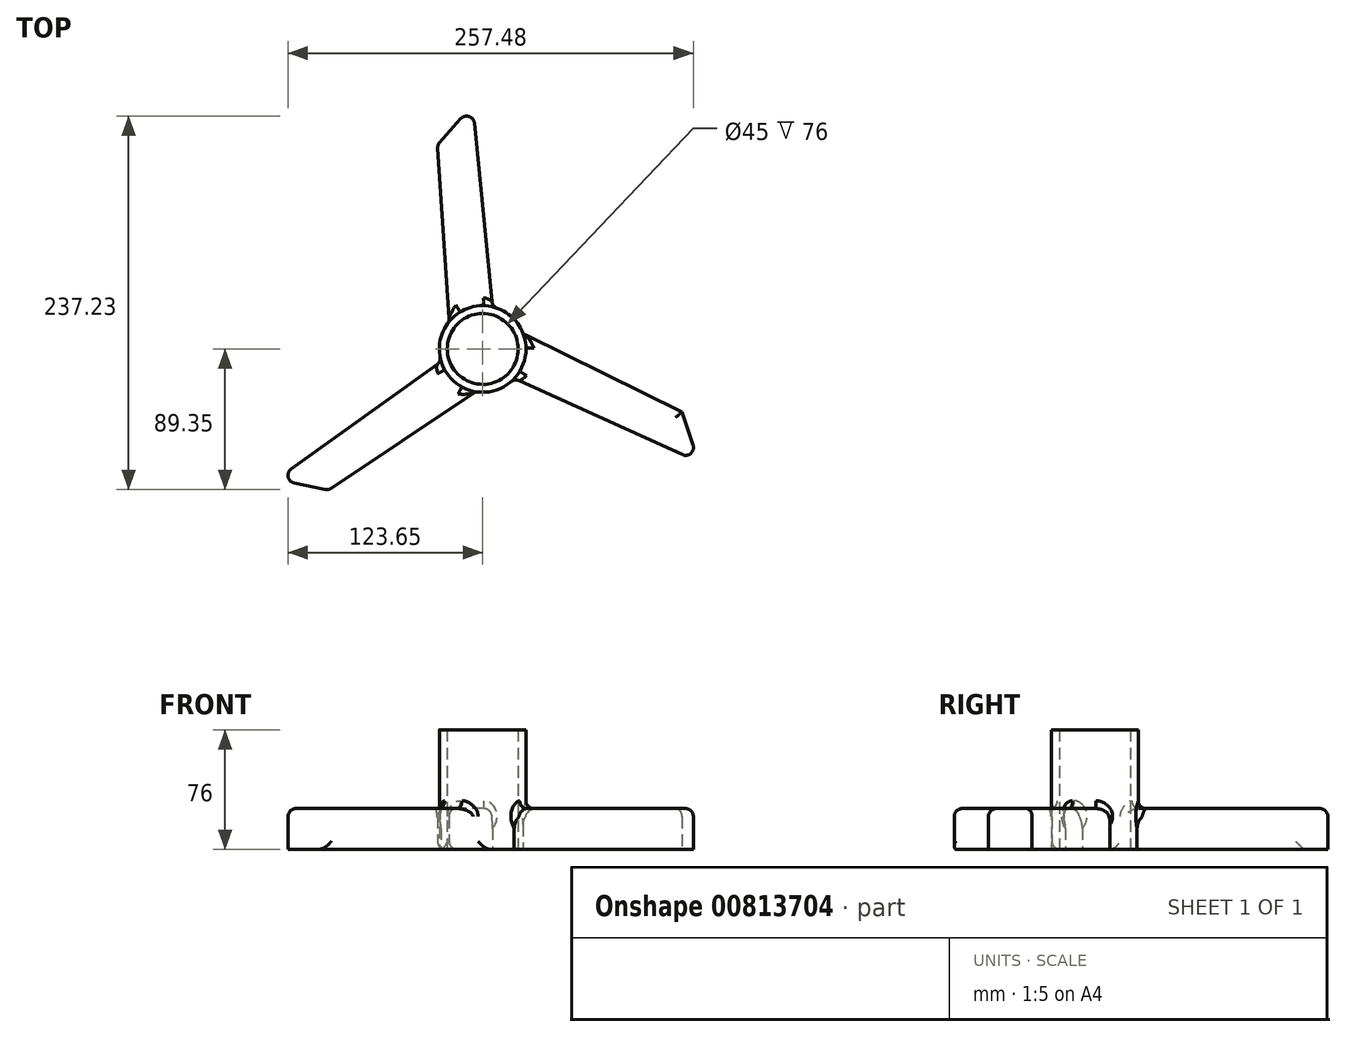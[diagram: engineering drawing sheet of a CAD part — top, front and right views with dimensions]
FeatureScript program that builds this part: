
annotation { "Feature Type Name" : "Feature", "Feature Type Description" : "" }
export const myFeature = defineFeature(function(context is Context, id is Id, definition is map)
    precondition{}
    {
        {
            var Q0;
            Q0=qCreatedBy(makeId("Top.planeOp"),FACE);
            var sketch = newSketch(context, id + "F0", { "sketchPlane" : qUnion([Q0])});
            skCircle(sketch, "E0", {"center": v(0, 0) * mm, "radius": 22.5 * mm});
            skLineSegment(sketch, "E1", {"start": v(-97.92, -89.67) * mm, "end": v(-4.54, -27.12) * mm});
            skCircle(sketch, "E2", {"center": v(0, 0) * mm, "radius": 27.5 * mm});
            skLineSegment(sketch, "E3", {"start": v(-26.31, -8) * mm, "end": v(-130.83, -82.84) * mm});
            skLineSegment(sketch, "E4", {"start": v(-130.83, -82.84) * mm, "end": v(-97.92, -89.67) * mm});
            skLineSegment(sketch, "E5.1.0", {"start": v(126.62, -39.97) * mm, "end": v(25.76, 9.63) * mm});
            skLineSegment(sketch, "E5.2.0", {"start": v(-28.7, 129.64) * mm, "end": v(-21.22, 17.5) * mm});
            skLineSegment(sketch, "E6.1.0", {"start": v(20.08, -18.79) * mm, "end": v(137.16, -71.89) * mm});
            skLineSegment(sketch, "E6.1.1", {"start": v(137.16, -71.89) * mm, "end": v(126.62, -39.97) * mm});
            skLineSegment(sketch, "E6.2.0", {"start": v(6.23, 26.79) * mm, "end": v(-6.32, 154.72) * mm});
            skLineSegment(sketch, "E6.2.1", {"start": v(-6.32, 154.72) * mm, "end": v(-28.7, 129.64) * mm});
            skSolve(sketch);
        }
        {
            var Q0;
            {var subQ0=sQuery(id+"F0.wireOp",EDGE,"E1");Q0=makeQuery(id+"F0.imprint","IMPRINT",FACE,{"disambiguationData":[TD([[makeQuery(id+"F0.imprint","IMPRINT",EDGE,{"derivedFrom":subQ0}),1.0]])]});}
            var Q1;
            Q1=makeQuery(id+"F0.imprint","IMPRINT",FACE,{"disambiguationData":[TD([[makeQuery(id+"F0.imprint","IMPRINT",EDGE,{"derivedFrom":sQuery(id+"F0.wireOp",EDGE,"E0")}),-1.0]])]});
            var Q2;
            {var subQ0=sQuery(id+"F0.wireOp",EDGE,"E6.1.0");Q2=makeQuery(id+"F0.imprint","IMPRINT",FACE,{"disambiguationData":[TD([[makeQuery(id+"F0.imprint","IMPRINT",EDGE,{"derivedFrom":subQ0}),1.0]])]});}
            var Q3;
            {var subQ0=sQuery(id+"F0.wireOp",EDGE,"E6.2.0");Q3=makeQuery(id+"F0.imprint","IMPRINT",FACE,{"disambiguationData":[TD([[makeQuery(id+"F0.imprint","IMPRINT",EDGE,{"derivedFrom":subQ0}),1.0]])]});}
            extrude(context, id + "F1", {"entities" : qUnion([Q0, Q1, Q2, Q3]), "depth" : 25.9 * mm, "offsetDistance" : 25 * mm});
        }
        {
            var Q0;
            Q0=makeQuery(id+"F0.imprint","IMPRINT",FACE,{"disambiguationData":[TD([[makeQuery(id+"F0.imprint","IMPRINT",EDGE,{"derivedFrom":sQuery(id+"F0.wireOp",EDGE,"E0")}),-1.0]])]});
            extrude(context, id + "F2", {"entities" : qUnion([Q0]), "operationType" : NewBodyOperationType.ADD, "depth" : 76 * mm, "offsetDistance" : 25 * mm});
        }
        {
            var Q0;
            {var subQ0=sQuery(id+"F0.wireOp",EDGE,"E6.2.0");var subQ1=sQuery(id+"F0.wireOp",EDGE,"E2");var subQ2=sQuery(id+"F0.wireOp",EDGE,"E1");var subQ3=sQuery(id+"F0.wireOp",EDGE,"E6.1.0");var subQ4=sQuery(id+"F0.wireOp",EDGE,"E3");var subQ5=sQuery(id+"F0.wireOp",EDGE,"E5.2.0");var subQ6=sQuery(id+"F0.wireOp",EDGE,"E5.1.0");var subQ7=sQuery(id+"F0.wireOp",EDGE,"E6.2.1");Q0=makeQuery(id+"F2.boolean.opBoolean","SPLIT",FACE,{"disambiguationData":[TD([makeQuery(id+"F1.opExtrude","SWEPT_FACE",FACE,{"disambiguationData":[OSD([subQ0])]})])],"derivedFrom":makeQuery(id+"F1.opExtrude","CAP_FACE",FACE,{"disambiguationData":[OSD([sQuery(id+"F0.wireOp",EDGE,"E0"),subQ2,subQ1,subQ4,sQuery(id+"F0.wireOp",EDGE,"E4"),subQ3,sQuery(id+"F0.wireOp",EDGE,"E6.1.1"),subQ6,subQ0,subQ7,subQ5])],"isStart":false})});}
            var Q1;
            {var subQ0=sQuery(id+"F0.wireOp",EDGE,"E2");var subQ1=sQuery(id+"F0.wireOp",EDGE,"E1");var subQ2=sQuery(id+"F0.wireOp",EDGE,"E6.1.0");var subQ3=sQuery(id+"F0.wireOp",EDGE,"E3");var subQ4=sQuery(id+"F0.wireOp",EDGE,"E5.2.0");var subQ5=sQuery(id+"F0.wireOp",EDGE,"E5.1.0");var subQ6=sQuery(id+"F0.wireOp",EDGE,"E6.2.0");var subQ7=sQuery(id+"F0.wireOp",EDGE,"E4");Q1=makeQuery(id+"F2.boolean.opBoolean","SPLIT",FACE,{"disambiguationData":[TD([makeQuery(id+"F1.opExtrude","SWEPT_FACE",FACE,{"disambiguationData":[OSD([subQ1])]})])],"derivedFrom":makeQuery(id+"F1.opExtrude","CAP_FACE",FACE,{"disambiguationData":[OSD([sQuery(id+"F0.wireOp",EDGE,"E0"),subQ1,subQ0,subQ3,subQ7,subQ2,sQuery(id+"F0.wireOp",EDGE,"E6.1.1"),subQ5,subQ6,sQuery(id+"F0.wireOp",EDGE,"E6.2.1"),subQ4])],"isStart":false})});}
            var Q2;
            {var subQ0=sQuery(id+"F0.wireOp",EDGE,"E2");var subQ1=sQuery(id+"F0.wireOp",EDGE,"E1");var subQ2=sQuery(id+"F0.wireOp",EDGE,"E6.1.0");var subQ3=sQuery(id+"F0.wireOp",EDGE,"E3");var subQ4=sQuery(id+"F0.wireOp",EDGE,"E5.2.0");var subQ5=sQuery(id+"F0.wireOp",EDGE,"E5.1.0");var subQ6=sQuery(id+"F0.wireOp",EDGE,"E6.2.0");var subQ7=sQuery(id+"F0.wireOp",EDGE,"E6.1.1");Q2=makeQuery(id+"F2.boolean.opBoolean","SPLIT",FACE,{"disambiguationData":[TD([makeQuery(id+"F1.opExtrude","SWEPT_FACE",FACE,{"disambiguationData":[OSD([subQ2])]})])],"derivedFrom":makeQuery(id+"F1.opExtrude","CAP_FACE",FACE,{"disambiguationData":[OSD([sQuery(id+"F0.wireOp",EDGE,"E0"),subQ1,subQ0,subQ3,sQuery(id+"F0.wireOp",EDGE,"E4"),subQ2,subQ7,subQ5,subQ6,sQuery(id+"F0.wireOp",EDGE,"E6.2.1"),subQ4])],"isStart":false})});}
            var Q3;
            Q3=makeQuery(id+"F1.opExtrude","SWEPT_EDGE",EDGE,{"disambiguationData":[OSD([sQuery(id+"F0.wireOp",EDGE,"E6.2.0"),sQuery(id+"F0.wireOp",EDGE,"E6.2.1")])]});
            var Q4;
            Q4=makeQuery(id+"F1.opExtrude","SWEPT_EDGE",EDGE,{"disambiguationData":[OSD([sQuery(id+"F0.wireOp",EDGE,"E6.2.1"),sQuery(id+"F0.wireOp",EDGE,"E5.2.0")])]});
            var Q5;
            Q5=makeQuery(id+"F1.opExtrude","SWEPT_EDGE",EDGE,{"disambiguationData":[OSD([sQuery(id+"F0.wireOp",EDGE,"E3"),sQuery(id+"F0.wireOp",EDGE,"E4")])]});
            var Q6;
            Q6=makeQuery(id+"F1.opExtrude","SWEPT_FACE",FACE,{"disambiguationData":[OSD([sQuery(id+"F0.wireOp",EDGE,"E1")])]});
            var Q7;
            Q7=makeQuery(id+"F1.opExtrude","SWEPT_EDGE",EDGE,{"disambiguationData":[OSD([sQuery(id+"F0.wireOp",EDGE,"E6.1.0"),sQuery(id+"F0.wireOp",EDGE,"E6.1.1")])]});
            var Q8;
            Q8=makeQuery(id+"F1.opExtrude","SWEPT_FACE",FACE,{"disambiguationData":[OSD([sQuery(id+"F0.wireOp",EDGE,"E5.1.0")])]});
            var Q9;
            Q9=makeQuery(id+"F1.opExtrude","SWEPT_FACE",FACE,{"disambiguationData":[OSD([sQuery(id+"F0.wireOp",EDGE,"E5.2.0")])]});
            fillet(context, id + "F3", {"entities" : qUnion([Q0, Q1, Q2, Q3, Q4, Q5, Q6, Q7, Q8, Q9]), "radius" : 5 * mm, "tangentPropagation" : true, "allowEdgeOverflow" : false});
        }
    });
